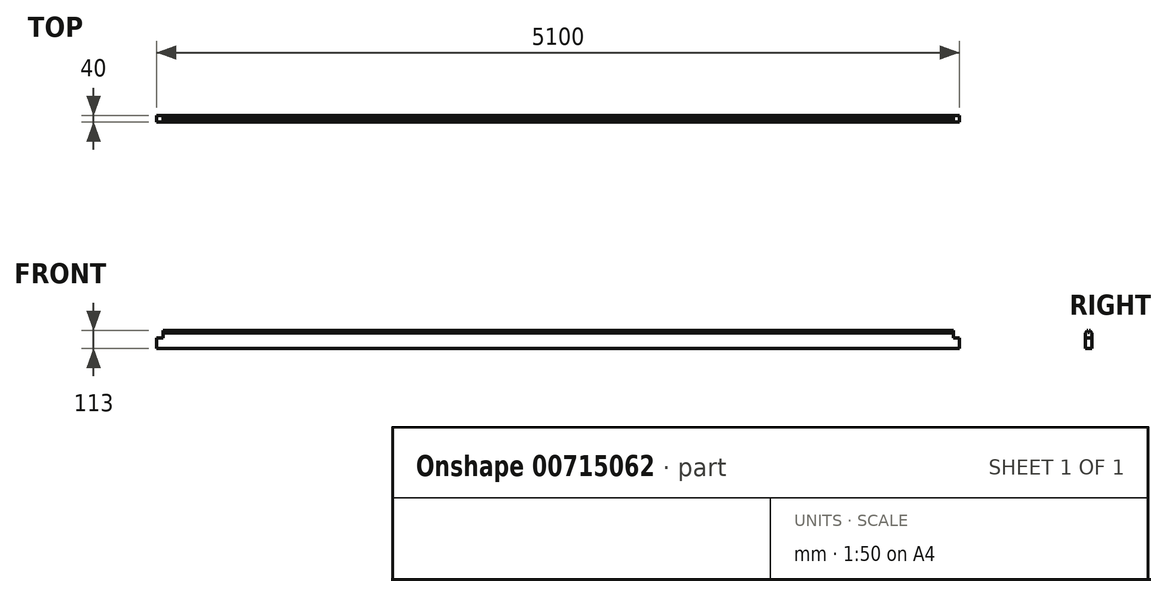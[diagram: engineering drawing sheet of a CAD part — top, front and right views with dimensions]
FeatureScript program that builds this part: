
annotation { "Feature Type Name" : "Feature", "Feature Type Description" : "" }
export const myFeature = defineFeature(function(context is Context, id is Id, definition is map)
    precondition{}
    {
        {
            assignVariable(context, id + "F0", {"name" : "Laenge", "anyValue" : 5100});
        }
        {
            var Q0;
            Q0=qCreatedBy(makeId("Right.planeOp"),FACE);
            var sketch = newSketch(context, id + "F1", { "sketchPlane" : qUnion([Q0])});
            skLineSegment(sketch, "E0", {"start": v(20, 63) * mm, "end": v(20, -63) * mm});
            skLineSegment(sketch, "E1", {"start": v(20, -63) * mm, "end": v(17, -66) * mm});
            skLineSegment(sketch, "E2", {"start": v(17, -66) * mm, "end": v(12, -66) * mm});
            skLineSegment(sketch, "E3", {"start": v(12, -52) * mm, "end": v(12, -66) * mm});
            skLineSegment(sketch, "E4", {"start": v(12, -52) * mm, "end": v(4, -52) * mm});
            skLineSegment(sketch, "E5", {"start": v(4, -66) * mm, "end": v(4, -52) * mm});
            skLineSegment(sketch, "E6", {"start": v(4, -66) * mm, "end": v(-4, -66) * mm});
            skLineSegment(sketch, "E7", {"start": v(-4, -52) * mm, "end": v(-4, -66) * mm});
            skLineSegment(sketch, "E8", {"start": v(-4, -52) * mm, "end": v(-12, -52) * mm});
            skLineSegment(sketch, "E9", {"start": v(-12, -66) * mm, "end": v(-12, -52) * mm});
            skLineSegment(sketch, "E10", {"start": v(-12, -66) * mm, "end": v(-17, -66) * mm});
            skLineSegment(sketch, "E11", {"start": v(-17, -66) * mm, "end": v(-20, -63) * mm});
            skLineSegment(sketch, "E12", {"start": v(-20, -63) * mm, "end": v(-20, 63) * mm});
            skLineSegment(sketch, "E13", {"start": v(-20, 63) * mm, "end": v(-17, 66) * mm});
            skLineSegment(sketch, "E14", {"start": v(-17, 66) * mm, "end": v(-12, 66) * mm});
            skLineSegment(sketch, "E15", {"start": v(-4, 66) * mm, "end": v(4, 66) * mm});
            skLineSegment(sketch, "E16", {"start": v(12, 66) * mm, "end": v(17, 66) * mm});
            skLineSegment(sketch, "E17", {"start": v(17, 66) * mm, "end": v(20, 63) * mm});
            skPoint(sketch, "E18.end.orphan", {"position": v(12, 57.8) * mm});
            skPoint(sketch, "E19.end.orphan", {"position": v(4, 66.3) * mm});
            skPoint(sketch, "E20.end.orphan", {"position": v(-4, 66.3) * mm});
            skLineSegment(sketch, "E21", {"start": v(-12, 66) * mm, "end": v(-12, 80) * mm});
            skLineSegment(sketch, "E22", {"start": v(-12, 80) * mm, "end": v(-4, 80) * mm});
            skLineSegment(sketch, "E23", {"start": v(-4, 80) * mm, "end": v(-4, 66) * mm});
            skLineSegment(sketch, "E24", {"start": v(4, 66) * mm, "end": v(4, 80) * mm});
            skLineSegment(sketch, "E25", {"start": v(4, 80) * mm, "end": v(12, 80) * mm});
            skLineSegment(sketch, "E26", {"start": v(12, 80) * mm, "end": v(12, 66) * mm});
            skLineSegment(sketch, "E27", {"start": v(20, -33) * mm, "end": v(-20, -33) * mm});
            skLineSegment(sketch, "E28", {"start": v(20, 33) * mm, "end": v(-20, 33) * mm});
            skPoint(sketch, "E29.end.orphan", {"position": v(-141.42, 0) * mm});
            skLineSegment(sketch, "E30", {"start": v(20, 0) * mm, "end": v(-20, 0) * mm});
            skLineSegment(sketch, "E31", {"start": v(20, 0) * mm, "end": v(-20, 0) * mm, "construction": true});
            skLineSegment(sketch, "E32", {"start": v(0, 33) * mm, "end": v(0, -33) * mm, "construction": true});
            skLineSegment(sketch, "E33", {"start": v(20, -52) * mm, "end": v(-20, -52) * mm});
            skSolve(sketch);
        }
        {
            var Q0;
            Q0=qCreatedBy(makeId("Front.planeOp"),FACE);
            var sketch = newSketch(context, id + "F2", { "sketchPlane" : qUnion([Q0])});
            skLineSegment(sketch, "E34", {"start": v(2550, 0) * mm, "end": v(-2550, 0) * mm, "construction": true});
            skPoint(sketch, "E35.right.start.orphan", {"position": v(-259.12, 108.1) * mm});
            skPoint(sketch, "E36.left.start.orphan", {"position": v(237.35, 108.1) * mm});
            skPoint(sketch, "E37.left.end.orphan", {"position": v(237.35, -84.05) * mm});
            skPoint(sketch, "E37.bottom.start.orphan", {"position": v(237.35, -117.05) * mm});
            skPoint(sketch, "E38.right.start.orphan", {"position": v(-259.12, -117.05) * mm});
            skPoint(sketch, "E38.top.end.orphan", {"position": v(-259.12, -84.05) * mm});
            skLineSegment(sketch, "E39.bottom", {"start": v(-2590, 33) * mm, "end": v(-2510, 33) * mm});
            skLineSegment(sketch, "E39.top", {"start": v(-2590, 133) * mm, "end": v(-2510, 133) * mm});
            skLineSegment(sketch, "E39.left", {"start": v(-2590, 33) * mm, "end": v(-2590, 133) * mm});
            skLineSegment(sketch, "E39.right", {"start": v(-2510, 33) * mm, "end": v(-2510, 133) * mm});
            skPoint(sketch, "E39.middle", {"position": v(-2550, 83) * mm});
            skLineSegment(sketch, "E40.bottom", {"start": v(-2590, -133) * mm, "end": v(-2510, -133) * mm});
            skLineSegment(sketch, "E40.top", {"start": v(-2590, -33) * mm, "end": v(-2510, -33) * mm});
            skLineSegment(sketch, "E40.left", {"start": v(-2590, -133) * mm, "end": v(-2590, -33) * mm});
            skLineSegment(sketch, "E40.right", {"start": v(-2510, -133) * mm, "end": v(-2510, -33) * mm});
            skPoint(sketch, "E40.middle", {"position": v(-2550, -83) * mm});
            skLineSegment(sketch, "E41.bottom", {"start": v(2590, 33) * mm, "end": v(2510, 33) * mm});
            skLineSegment(sketch, "E41.top", {"start": v(2590, 133) * mm, "end": v(2510, 133) * mm});
            skLineSegment(sketch, "E41.left", {"start": v(2590, 33) * mm, "end": v(2590, 133) * mm});
            skLineSegment(sketch, "E41.right", {"start": v(2510, 33) * mm, "end": v(2510, 133) * mm});
            skPoint(sketch, "E41.middle", {"position": v(2550, 83) * mm});
            skLineSegment(sketch, "E42.bottom", {"start": v(2590, -33) * mm, "end": v(2510, -33) * mm});
            skLineSegment(sketch, "E42.top", {"start": v(2590, -133) * mm, "end": v(2510, -133) * mm});
            skLineSegment(sketch, "E42.left", {"start": v(2590, -33) * mm, "end": v(2590, -133) * mm});
            skLineSegment(sketch, "E42.right", {"start": v(2510, -33) * mm, "end": v(2510, -133) * mm});
            skPoint(sketch, "E42.middle", {"position": v(2550, -83) * mm});
            skSolve(sketch);
        }
        {
            var Q0;
            {var subQ3=sQuery(id+"F1.wireOp",EDGE,"E13");Q0=makeQuery(id+"F1.imprint","IMPRINT",FACE,{"disambiguationData":[TD([[makeQuery(id+"F1.imprint","IMPRINT",EDGE,{"derivedFrom":subQ3}),-1.0]])]});}
            var Q1;
            {var subQ0=sQuery(id+"F1.wireOp",EDGE,"E28");Q1=makeQuery(id+"F1.imprint","IMPRINT",FACE,{"disambiguationData":[TD([[makeQuery(id+"F1.imprint","IMPRINT",EDGE,{"derivedFrom":subQ0}),1.0]])]});}
            var Q2;
            {var subQ0=sQuery(id+"F1.wireOp",EDGE,"E27");Q2=makeQuery(id+"F1.imprint","IMPRINT",FACE,{"disambiguationData":[TD([[makeQuery(id+"F1.imprint","IMPRINT",EDGE,{"derivedFrom":subQ0}),-1.0]])]});}
            var Q3;
            {var subQ0=sQuery(id+"F1.wireOp",EDGE,"E27");Q3=makeQuery(id+"F1.imprint","IMPRINT",FACE,{"disambiguationData":[TD([[makeQuery(id+"F1.imprint","IMPRINT",EDGE,{"derivedFrom":subQ0}),1.0]])]});}
            extrude(context, id + "F3", {"entities" : qUnion([Q0, Q1, Q2, Q3]), "endBound" : BoundingType.SYMMETRIC, "depth" : getVariable(context, 'Laenge') * mm, "offsetDistance" : 25 * mm});
        }
        {
            var Q0;
            Q0=makeQuery(id+"F2.imprint","IMPRINT",FACE,{"disambiguationData":[TD([[makeQuery(id+"F2.imprint","IMPRINT",EDGE,{"derivedFrom":sQuery(id+"F2.wireOp",EDGE,"E39.bottom")}),1.0]])]});
            var Q1;
            Q1=makeQuery(id+"F2.imprint","IMPRINT",FACE,{"disambiguationData":[TD([[makeQuery(id+"F2.imprint","IMPRINT",EDGE,{"derivedFrom":sQuery(id+"F2.wireOp",EDGE,"E40.bottom")}),1.0]])]});
            var Q2;
            Q2=makeQuery(id+"F2.imprint","IMPRINT",FACE,{"disambiguationData":[TD([[makeQuery(id+"F2.imprint","IMPRINT",EDGE,{"derivedFrom":sQuery(id+"F2.wireOp",EDGE,"E41.bottom")}),-1.0]])]});
            var Q3;
            Q3=makeQuery(id+"F2.imprint","IMPRINT",FACE,{"disambiguationData":[TD([[makeQuery(id+"F2.imprint","IMPRINT",EDGE,{"derivedFrom":sQuery(id+"F2.wireOp",EDGE,"E42.bottom")}),1.0]])]});
            extrude(context, id + "F4", {"entities" : qUnion([Q0, Q1, Q2, Q3]), "operationType" : NewBodyOperationType.REMOVE, "endBound" : BoundingType.SYMMETRIC, "depth" : 50 * mm, "offsetDistance" : 25 * mm});
        }
        {
            var Q0;
            Q0=makeQuery(id+"F3.opExtrude","SWEPT_FACE",FACE,{"disambiguationData":[OSD([sQuery(id+"F1.wireOp",EDGE,"E12")])]});
            var sketch = newSketch(context, id + "F5", { "sketchPlane" : qUnion([Q0])});
            skLineSegment(sketch, "E43.bottom", {"start": v(-2550, -33) * mm, "end": v(2510, -33) * mm});
            skLineSegment(sketch, "E43.top", {"start": v(-2550, -52) * mm, "end": v(2510, -52) * mm});
            skLineSegment(sketch, "E43.left", {"start": v(-2550, -33) * mm, "end": v(-2550, -52) * mm});
            skLineSegment(sketch, "E43.right", {"start": v(2510, -33) * mm, "end": v(2510, -52) * mm});
            skSolve(sketch);
        }
        {
            var Q0;
            {var subQ3=sQuery(id+"F5.wireOp",EDGE,"E43.right");Q0=makeQuery(id+"F5.imprint","IMPRINT",FACE,{"disambiguationData":[TD([[makeQuery(id+"F5.imprint","IMPRINT",EDGE,{"derivedFrom":subQ3}),1.0]])]});}
            extrude(context, id + "F6", {"entities" : qUnion([Q0]), "operationType" : NewBodyOperationType.REMOVE, "endBound" : BoundingType.UP_TO_NEXT, "oppositeDirection" : true, "depth" : 25 * mm, "offsetDistance" : 25 * mm});
        }
    });
